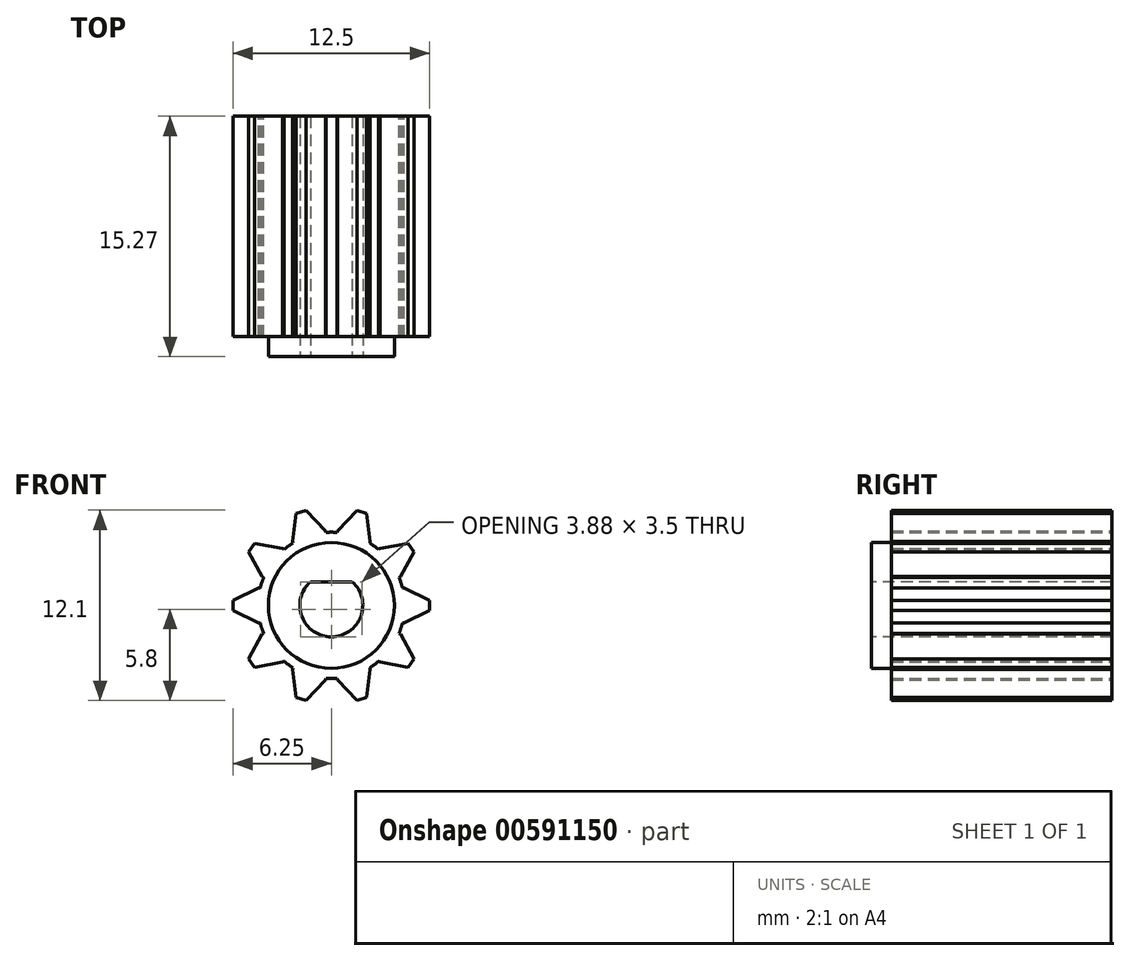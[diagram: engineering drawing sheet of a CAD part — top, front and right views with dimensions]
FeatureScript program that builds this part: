
annotation { "Feature Type Name" : "Feature", "Feature Type Description" : "" }
export const myFeature = defineFeature(function(context is Context, id is Id, definition is map)
    precondition{}
    {
        {
            var Q0;
            Q0=qCreatedBy(makeId("Front.planeOp"),FACE);
            var sketch = newSketch(context, id + "F0", { "sketchPlane" : qUnion([Q0])});
            skCircle(sketch, "E0", {"center": v(0, 0) * mm, "radius": 4.65 * mm});
            skLineSegment(sketch, "E1", {"start": v(0, 0) * mm, "end": v(4.65, 0) * mm, "construction": true});
            skLineSegment(sketch, "E2", {"start": v(4.65, 0) * mm, "end": v(6.25, 0) * mm, "construction": true});
            skLineSegment(sketch, "E3", {"start": v(6.25, 0) * mm, "end": v(6.25, 0.33) * mm});
            skLineSegment(sketch, "E4", {"start": v(4.52, 1.1) * mm, "end": v(4.62, 1.1) * mm});
            skLineSegment(sketch, "E5", {"start": v(4.62, 1.1) * mm, "end": v(6.25, 0.33) * mm});
            skLineSegment(sketch, "E6.MirrorCS", {"start": v(4.62, -1.1) * mm, "end": v(6.25, -0.33) * mm});
            skLineSegment(sketch, "E7.MirrorCS", {"start": v(6.25, 0) * mm, "end": v(6.25, -0.33) * mm});
            skLineSegment(sketch, "E8.MirrorCS", {"start": v(4.52, -1.1) * mm, "end": v(4.62, -1.1) * mm});
            skLineSegment(sketch, "E9.1.0", {"start": v(3, 3.55) * mm, "end": v(3.09, 3.6) * mm});
            skLineSegment(sketch, "E9.1.1", {"start": v(4.3, 1.77) * mm, "end": v(4.38, 1.82) * mm});
            skLineSegment(sketch, "E9.1.2", {"start": v(4.38, 1.82) * mm, "end": v(5.25, 3.4) * mm});
            skLineSegment(sketch, "E9.1.3", {"start": v(3.09, 3.6) * mm, "end": v(4.86, 3.94) * mm});
            skLineSegment(sketch, "E9.1.4", {"start": v(5.06, 3.67) * mm, "end": v(4.86, 3.94) * mm});
            skLineSegment(sketch, "E9.1.5", {"start": v(5.06, 3.67) * mm, "end": v(5.25, 3.4) * mm});
            skLineSegment(sketch, "E9.2.0", {"start": v(0.35, 4.64) * mm, "end": v(0.38, 4.73) * mm});
            skLineSegment(sketch, "E9.2.1", {"start": v(2.44, 3.96) * mm, "end": v(2.47, 4.05) * mm});
            skLineSegment(sketch, "E9.2.2", {"start": v(2.47, 4.05) * mm, "end": v(2.25, 5.84) * mm});
            skLineSegment(sketch, "E9.2.3", {"start": v(0.38, 4.73) * mm, "end": v(1.62, 6.05) * mm});
            skLineSegment(sketch, "E9.2.4", {"start": v(1.93, 5.94) * mm, "end": v(1.62, 6.05) * mm});
            skLineSegment(sketch, "E9.2.5", {"start": v(1.93, 5.94) * mm, "end": v(2.25, 5.84) * mm});
            skLineSegment(sketch, "E9.3.0", {"start": v(-2.44, 3.96) * mm, "end": v(-2.47, 4.05) * mm});
            skLineSegment(sketch, "E9.3.1", {"start": v(-0.35, 4.64) * mm, "end": v(-0.38, 4.73) * mm});
            skLineSegment(sketch, "E9.3.2", {"start": v(-0.38, 4.73) * mm, "end": v(-1.62, 6.05) * mm});
            skLineSegment(sketch, "E9.3.3", {"start": v(-2.47, 4.05) * mm, "end": v(-2.25, 5.84) * mm});
            skLineSegment(sketch, "E9.3.4", {"start": v(-1.93, 5.94) * mm, "end": v(-2.25, 5.84) * mm});
            skLineSegment(sketch, "E9.3.5", {"start": v(-1.93, 5.94) * mm, "end": v(-1.62, 6.05) * mm});
            skLineSegment(sketch, "E9.4.0", {"start": v(-4.3, 1.77) * mm, "end": v(-4.38, 1.82) * mm});
            skLineSegment(sketch, "E9.4.1", {"start": v(-3, 3.55) * mm, "end": v(-3.09, 3.6) * mm});
            skLineSegment(sketch, "E9.4.2", {"start": v(-3.09, 3.6) * mm, "end": v(-4.86, 3.94) * mm});
            skLineSegment(sketch, "E9.4.3", {"start": v(-4.38, 1.82) * mm, "end": v(-5.25, 3.4) * mm});
            skLineSegment(sketch, "E9.4.4", {"start": v(-5.06, 3.67) * mm, "end": v(-5.25, 3.4) * mm});
            skLineSegment(sketch, "E9.4.5", {"start": v(-5.06, 3.67) * mm, "end": v(-4.86, 3.94) * mm});
            skLineSegment(sketch, "E9.5.0", {"start": v(-4.52, -1.1) * mm, "end": v(-4.62, -1.1) * mm});
            skLineSegment(sketch, "E9.5.1", {"start": v(-4.52, 1.1) * mm, "end": v(-4.62, 1.1) * mm});
            skLineSegment(sketch, "E9.5.2", {"start": v(-4.62, 1.1) * mm, "end": v(-6.25, 0.33) * mm});
            skLineSegment(sketch, "E9.5.3", {"start": v(-4.62, -1.1) * mm, "end": v(-6.25, -0.33) * mm});
            skLineSegment(sketch, "E9.5.4", {"start": v(-6.25, 0) * mm, "end": v(-6.25, -0.33) * mm});
            skLineSegment(sketch, "E9.5.5", {"start": v(-6.25, 0) * mm, "end": v(-6.25, 0.33) * mm});
            skLineSegment(sketch, "E9.6.0", {"start": v(-3, -3.55) * mm, "end": v(-3.09, -3.6) * mm});
            skLineSegment(sketch, "E9.6.1", {"start": v(-4.3, -1.77) * mm, "end": v(-4.38, -1.82) * mm});
            skLineSegment(sketch, "E9.6.2", {"start": v(-4.38, -1.82) * mm, "end": v(-5.25, -3.4) * mm});
            skLineSegment(sketch, "E9.6.3", {"start": v(-3.09, -3.6) * mm, "end": v(-4.86, -3.94) * mm});
            skLineSegment(sketch, "E9.6.4", {"start": v(-5.06, -3.67) * mm, "end": v(-4.86, -3.94) * mm});
            skLineSegment(sketch, "E9.6.5", {"start": v(-5.06, -3.67) * mm, "end": v(-5.25, -3.4) * mm});
            skLineSegment(sketch, "E9.7.0", {"start": v(-0.35, -4.64) * mm, "end": v(-0.38, -4.73) * mm});
            skLineSegment(sketch, "E9.7.1", {"start": v(-2.44, -3.96) * mm, "end": v(-2.47, -4.05) * mm});
            skLineSegment(sketch, "E9.7.2", {"start": v(-2.47, -4.05) * mm, "end": v(-2.25, -5.84) * mm});
            skLineSegment(sketch, "E9.7.3", {"start": v(-0.38, -4.73) * mm, "end": v(-1.62, -6.05) * mm});
            skLineSegment(sketch, "E9.7.4", {"start": v(-1.93, -5.94) * mm, "end": v(-1.62, -6.05) * mm});
            skLineSegment(sketch, "E9.7.5", {"start": v(-1.93, -5.94) * mm, "end": v(-2.25, -5.84) * mm});
            skLineSegment(sketch, "E9.8.0", {"start": v(2.44, -3.96) * mm, "end": v(2.47, -4.05) * mm});
            skLineSegment(sketch, "E9.8.1", {"start": v(0.35, -4.64) * mm, "end": v(0.38, -4.73) * mm});
            skLineSegment(sketch, "E9.8.2", {"start": v(0.38, -4.73) * mm, "end": v(1.62, -6.05) * mm});
            skLineSegment(sketch, "E9.8.3", {"start": v(2.47, -4.05) * mm, "end": v(2.25, -5.84) * mm});
            skLineSegment(sketch, "E9.8.4", {"start": v(1.93, -5.94) * mm, "end": v(2.25, -5.84) * mm});
            skLineSegment(sketch, "E9.8.5", {"start": v(1.93, -5.94) * mm, "end": v(1.62, -6.05) * mm});
            skLineSegment(sketch, "E9.9.0", {"start": v(4.3, -1.77) * mm, "end": v(4.38, -1.82) * mm});
            skLineSegment(sketch, "E9.9.1", {"start": v(3, -3.55) * mm, "end": v(3.09, -3.6) * mm});
            skLineSegment(sketch, "E9.9.2", {"start": v(3.09, -3.6) * mm, "end": v(4.86, -3.94) * mm});
            skLineSegment(sketch, "E9.9.3", {"start": v(4.38, -1.82) * mm, "end": v(5.25, -3.4) * mm});
            skLineSegment(sketch, "E9.9.4", {"start": v(5.06, -3.67) * mm, "end": v(5.25, -3.4) * mm});
            skLineSegment(sketch, "E9.9.5", {"start": v(5.06, -3.67) * mm, "end": v(4.86, -3.94) * mm});
            skSolve(sketch);
        }
        {
            var Q0;
            Q0 = qSketchRegion(id + "F0", true);
            extrude(context, id + "F1", {"entities" : qUnion([Q0]), "depth" : 9 * mm, "offsetDistance" : 25.4 * mm, "hasSecondDirection" : true, "secondDirectionOppositeDirection" : true, "secondDirectionDepth" : 5 * mm});
        }
        {
            var Q0;
            Q0=makeQuery(id+"F1.opExtrude","CAP_FACE",FACE,{"disambiguationData":[OSD([sQuery(id+"F0.wireOp",EDGE,"E0"),sQuery(id+"F0.wireOp",EDGE,"E3"),sQuery(id+"F0.wireOp",EDGE,"E4"),sQuery(id+"F0.wireOp",EDGE,"E5"),sQuery(id+"F0.wireOp",EDGE,"E6.MirrorCS"),sQuery(id+"F0.wireOp",EDGE,"E7.MirrorCS"),sQuery(id+"F0.wireOp",EDGE,"E8.MirrorCS"),sQuery(id+"F0.wireOp",EDGE,"9f6130ec-3d1a-4bbb-9d9a-4e7b52390a97.1.0"),sQuery(id+"F0.wireOp",EDGE,"9f6130ec-3d1a-4bbb-9d9a-4e7b52390a97.1.1"),sQuery(id+"F0.wireOp",EDGE,"9f6130ec-3d1a-4bbb-9d9a-4e7b52390a97.1.2"),sQuery(id+"F0.wireOp",EDGE,"9f6130ec-3d1a-4bbb-9d9a-4e7b52390a97.1.3"),sQuery(id+"F0.wireOp",EDGE,"9f6130ec-3d1a-4bbb-9d9a-4e7b52390a97.1.4"),sQuery(id+"F0.wireOp",EDGE,"9f6130ec-3d1a-4bbb-9d9a-4e7b52390a97.1.5"),sQuery(id+"F0.wireOp",EDGE,"9f6130ec-3d1a-4bbb-9d9a-4e7b52390a97.2.0"),sQuery(id+"F0.wireOp",EDGE,"9f6130ec-3d1a-4bbb-9d9a-4e7b52390a97.2.1"),sQuery(id+"F0.wireOp",EDGE,"9f6130ec-3d1a-4bbb-9d9a-4e7b52390a97.2.2"),sQuery(id+"F0.wireOp",EDGE,"9f6130ec-3d1a-4bbb-9d9a-4e7b52390a97.2.3"),sQuery(id+"F0.wireOp",EDGE,"9f6130ec-3d1a-4bbb-9d9a-4e7b52390a97.2.4"),sQuery(id+"F0.wireOp",EDGE,"9f6130ec-3d1a-4bbb-9d9a-4e7b52390a97.2.5"),sQuery(id+"F0.wireOp",EDGE,"9f6130ec-3d1a-4bbb-9d9a-4e7b52390a97.3.0"),sQuery(id+"F0.wireOp",EDGE,"9f6130ec-3d1a-4bbb-9d9a-4e7b52390a97.3.1"),sQuery(id+"F0.wireOp",EDGE,"9f6130ec-3d1a-4bbb-9d9a-4e7b52390a97.3.2"),sQuery(id+"F0.wireOp",EDGE,"9f6130ec-3d1a-4bbb-9d9a-4e7b52390a97.3.3"),sQuery(id+"F0.wireOp",EDGE,"9f6130ec-3d1a-4bbb-9d9a-4e7b52390a97.3.4"),sQuery(id+"F0.wireOp",EDGE,"9f6130ec-3d1a-4bbb-9d9a-4e7b52390a97.3.5"),sQuery(id+"F0.wireOp",EDGE,"9f6130ec-3d1a-4bbb-9d9a-4e7b52390a97.4.0"),sQuery(id+"F0.wireOp",EDGE,"9f6130ec-3d1a-4bbb-9d9a-4e7b52390a97.4.1"),sQuery(id+"F0.wireOp",EDGE,"9f6130ec-3d1a-4bbb-9d9a-4e7b52390a97.4.2"),sQuery(id+"F0.wireOp",EDGE,"9f6130ec-3d1a-4bbb-9d9a-4e7b52390a97.4.3"),sQuery(id+"F0.wireOp",EDGE,"9f6130ec-3d1a-4bbb-9d9a-4e7b52390a97.4.4"),sQuery(id+"F0.wireOp",EDGE,"9f6130ec-3d1a-4bbb-9d9a-4e7b52390a97.4.5"),sQuery(id+"F0.wireOp",EDGE,"9f6130ec-3d1a-4bbb-9d9a-4e7b52390a97.5.0"),sQuery(id+"F0.wireOp",EDGE,"9f6130ec-3d1a-4bbb-9d9a-4e7b52390a97.5.1"),sQuery(id+"F0.wireOp",EDGE,"9f6130ec-3d1a-4bbb-9d9a-4e7b52390a97.5.2"),sQuery(id+"F0.wireOp",EDGE,"9f6130ec-3d1a-4bbb-9d9a-4e7b52390a97.5.3"),sQuery(id+"F0.wireOp",EDGE,"9f6130ec-3d1a-4bbb-9d9a-4e7b52390a97.5.4"),sQuery(id+"F0.wireOp",EDGE,"9f6130ec-3d1a-4bbb-9d9a-4e7b52390a97.5.5"),sQuery(id+"F0.wireOp",EDGE,"9f6130ec-3d1a-4bbb-9d9a-4e7b52390a97.6.0"),sQuery(id+"F0.wireOp",EDGE,"9f6130ec-3d1a-4bbb-9d9a-4e7b52390a97.6.1"),sQuery(id+"F0.wireOp",EDGE,"9f6130ec-3d1a-4bbb-9d9a-4e7b52390a97.6.2"),sQuery(id+"F0.wireOp",EDGE,"9f6130ec-3d1a-4bbb-9d9a-4e7b52390a97.6.3"),sQuery(id+"F0.wireOp",EDGE,"9f6130ec-3d1a-4bbb-9d9a-4e7b52390a97.6.4"),sQuery(id+"F0.wireOp",EDGE,"9f6130ec-3d1a-4bbb-9d9a-4e7b52390a97.6.5"),sQuery(id+"F0.wireOp",EDGE,"9f6130ec-3d1a-4bbb-9d9a-4e7b52390a97.7.0"),sQuery(id+"F0.wireOp",EDGE,"9f6130ec-3d1a-4bbb-9d9a-4e7b52390a97.7.1"),sQuery(id+"F0.wireOp",EDGE,"9f6130ec-3d1a-4bbb-9d9a-4e7b52390a97.7.2"),sQuery(id+"F0.wireOp",EDGE,"9f6130ec-3d1a-4bbb-9d9a-4e7b52390a97.7.3"),sQuery(id+"F0.wireOp",EDGE,"9f6130ec-3d1a-4bbb-9d9a-4e7b52390a97.7.4"),sQuery(id+"F0.wireOp",EDGE,"9f6130ec-3d1a-4bbb-9d9a-4e7b52390a97.7.5"),sQuery(id+"F0.wireOp",EDGE,"9f6130ec-3d1a-4bbb-9d9a-4e7b52390a97.8.0"),sQuery(id+"F0.wireOp",EDGE,"9f6130ec-3d1a-4bbb-9d9a-4e7b52390a97.8.1"),sQuery(id+"F0.wireOp",EDGE,"9f6130ec-3d1a-4bbb-9d9a-4e7b52390a97.8.2"),sQuery(id+"F0.wireOp",EDGE,"9f6130ec-3d1a-4bbb-9d9a-4e7b52390a97.8.3"),sQuery(id+"F0.wireOp",EDGE,"9f6130ec-3d1a-4bbb-9d9a-4e7b52390a97.8.4"),sQuery(id+"F0.wireOp",EDGE,"9f6130ec-3d1a-4bbb-9d9a-4e7b52390a97.8.5"),sQuery(id+"F0.wireOp",EDGE,"9f6130ec-3d1a-4bbb-9d9a-4e7b52390a97.9.0"),sQuery(id+"F0.wireOp",EDGE,"9f6130ec-3d1a-4bbb-9d9a-4e7b52390a97.9.1"),sQuery(id+"F0.wireOp",EDGE,"9f6130ec-3d1a-4bbb-9d9a-4e7b52390a97.9.2"),sQuery(id+"F0.wireOp",EDGE,"9f6130ec-3d1a-4bbb-9d9a-4e7b52390a97.9.3"),sQuery(id+"F0.wireOp",EDGE,"9f6130ec-3d1a-4bbb-9d9a-4e7b52390a97.9.4"),sQuery(id+"F0.wireOp",EDGE,"9f6130ec-3d1a-4bbb-9d9a-4e7b52390a97.9.5"),sQuery(id+"F0.wireOp",EDGE,"9f6130ec-3d1a-4bbb-9d9a-4e7b52390a97.10.0"),sQuery(id+"F0.wireOp",EDGE,"9f6130ec-3d1a-4bbb-9d9a-4e7b52390a97.10.1"),sQuery(id+"F0.wireOp",EDGE,"9f6130ec-3d1a-4bbb-9d9a-4e7b52390a97.10.2"),sQuery(id+"F0.wireOp",EDGE,"9f6130ec-3d1a-4bbb-9d9a-4e7b52390a97.10.3"),sQuery(id+"F0.wireOp",EDGE,"9f6130ec-3d1a-4bbb-9d9a-4e7b52390a97.10.4"),sQuery(id+"F0.wireOp",EDGE,"9f6130ec-3d1a-4bbb-9d9a-4e7b52390a97.10.5"),sQuery(id+"F0.wireOp",EDGE,"9f6130ec-3d1a-4bbb-9d9a-4e7b52390a97.11.0"),sQuery(id+"F0.wireOp",EDGE,"9f6130ec-3d1a-4bbb-9d9a-4e7b52390a97.11.1"),sQuery(id+"F0.wireOp",EDGE,"9f6130ec-3d1a-4bbb-9d9a-4e7b52390a97.11.2"),sQuery(id+"F0.wireOp",EDGE,"9f6130ec-3d1a-4bbb-9d9a-4e7b52390a97.11.3"),sQuery(id+"F0.wireOp",EDGE,"9f6130ec-3d1a-4bbb-9d9a-4e7b52390a97.11.4"),sQuery(id+"F0.wireOp",EDGE,"9f6130ec-3d1a-4bbb-9d9a-4e7b52390a97.11.5"),sQuery(id+"F0.wireOp",EDGE,"9f6130ec-3d1a-4bbb-9d9a-4e7b52390a97.12.0"),sQuery(id+"F0.wireOp",EDGE,"9f6130ec-3d1a-4bbb-9d9a-4e7b52390a97.12.1"),sQuery(id+"F0.wireOp",EDGE,"9f6130ec-3d1a-4bbb-9d9a-4e7b52390a97.12.2"),sQuery(id+"F0.wireOp",EDGE,"9f6130ec-3d1a-4bbb-9d9a-4e7b52390a97.12.3"),sQuery(id+"F0.wireOp",EDGE,"9f6130ec-3d1a-4bbb-9d9a-4e7b52390a97.12.4"),sQuery(id+"F0.wireOp",EDGE,"9f6130ec-3d1a-4bbb-9d9a-4e7b52390a97.12.5"),sQuery(id+"F0.wireOp",EDGE,"9f6130ec-3d1a-4bbb-9d9a-4e7b52390a97.13.0"),sQuery(id+"F0.wireOp",EDGE,"9f6130ec-3d1a-4bbb-9d9a-4e7b52390a97.13.1"),sQuery(id+"F0.wireOp",EDGE,"9f6130ec-3d1a-4bbb-9d9a-4e7b52390a97.13.2"),sQuery(id+"F0.wireOp",EDGE,"9f6130ec-3d1a-4bbb-9d9a-4e7b52390a97.13.3"),sQuery(id+"F0.wireOp",EDGE,"9f6130ec-3d1a-4bbb-9d9a-4e7b52390a97.13.4"),sQuery(id+"F0.wireOp",EDGE,"9f6130ec-3d1a-4bbb-9d9a-4e7b52390a97.13.5"),sQuery(id+"F0.wireOp",EDGE,"9f6130ec-3d1a-4bbb-9d9a-4e7b52390a97.14.0"),sQuery(id+"F0.wireOp",EDGE,"9f6130ec-3d1a-4bbb-9d9a-4e7b52390a97.14.1"),sQuery(id+"F0.wireOp",EDGE,"9f6130ec-3d1a-4bbb-9d9a-4e7b52390a97.14.2"),sQuery(id+"F0.wireOp",EDGE,"9f6130ec-3d1a-4bbb-9d9a-4e7b52390a97.14.3"),sQuery(id+"F0.wireOp",EDGE,"9f6130ec-3d1a-4bbb-9d9a-4e7b52390a97.14.4"),sQuery(id+"F0.wireOp",EDGE,"9f6130ec-3d1a-4bbb-9d9a-4e7b52390a97.14.5"),sQuery(id+"F0.wireOp",EDGE,"9f6130ec-3d1a-4bbb-9d9a-4e7b52390a97.15.0"),sQuery(id+"F0.wireOp",EDGE,"9f6130ec-3d1a-4bbb-9d9a-4e7b52390a97.15.1"),sQuery(id+"F0.wireOp",EDGE,"9f6130ec-3d1a-4bbb-9d9a-4e7b52390a97.15.2"),sQuery(id+"F0.wireOp",EDGE,"9f6130ec-3d1a-4bbb-9d9a-4e7b52390a97.15.3"),sQuery(id+"F0.wireOp",EDGE,"9f6130ec-3d1a-4bbb-9d9a-4e7b52390a97.15.4"),sQuery(id+"F0.wireOp",EDGE,"9f6130ec-3d1a-4bbb-9d9a-4e7b52390a97.15.5"),sQuery(id+"F0.wireOp",EDGE,"9f6130ec-3d1a-4bbb-9d9a-4e7b52390a97.16.0"),sQuery(id+"F0.wireOp",EDGE,"9f6130ec-3d1a-4bbb-9d9a-4e7b52390a97.16.1"),sQuery(id+"F0.wireOp",EDGE,"9f6130ec-3d1a-4bbb-9d9a-4e7b52390a97.16.2"),sQuery(id+"F0.wireOp",EDGE,"9f6130ec-3d1a-4bbb-9d9a-4e7b52390a97.16.3"),sQuery(id+"F0.wireOp",EDGE,"9f6130ec-3d1a-4bbb-9d9a-4e7b52390a97.16.4"),sQuery(id+"F0.wireOp",EDGE,"9f6130ec-3d1a-4bbb-9d9a-4e7b52390a97.16.5"),sQuery(id+"F0.wireOp",EDGE,"9f6130ec-3d1a-4bbb-9d9a-4e7b52390a97.17.0"),sQuery(id+"F0.wireOp",EDGE,"9f6130ec-3d1a-4bbb-9d9a-4e7b52390a97.17.1"),sQuery(id+"F0.wireOp",EDGE,"9f6130ec-3d1a-4bbb-9d9a-4e7b52390a97.17.2"),sQuery(id+"F0.wireOp",EDGE,"9f6130ec-3d1a-4bbb-9d9a-4e7b52390a97.17.3"),sQuery(id+"F0.wireOp",EDGE,"9f6130ec-3d1a-4bbb-9d9a-4e7b52390a97.17.4"),sQuery(id+"F0.wireOp",EDGE,"9f6130ec-3d1a-4bbb-9d9a-4e7b52390a97.17.5"),sQuery(id+"F0.wireOp",EDGE,"9f6130ec-3d1a-4bbb-9d9a-4e7b52390a97.18.0"),sQuery(id+"F0.wireOp",EDGE,"9f6130ec-3d1a-4bbb-9d9a-4e7b52390a97.18.1"),sQuery(id+"F0.wireOp",EDGE,"9f6130ec-3d1a-4bbb-9d9a-4e7b52390a97.18.2"),sQuery(id+"F0.wireOp",EDGE,"9f6130ec-3d1a-4bbb-9d9a-4e7b52390a97.18.3"),sQuery(id+"F0.wireOp",EDGE,"9f6130ec-3d1a-4bbb-9d9a-4e7b52390a97.18.4"),sQuery(id+"F0.wireOp",EDGE,"9f6130ec-3d1a-4bbb-9d9a-4e7b52390a97.18.5"),sQuery(id+"F0.wireOp",EDGE,"9f6130ec-3d1a-4bbb-9d9a-4e7b52390a97.19.0"),sQuery(id+"F0.wireOp",EDGE,"9f6130ec-3d1a-4bbb-9d9a-4e7b52390a97.19.1"),sQuery(id+"F0.wireOp",EDGE,"9f6130ec-3d1a-4bbb-9d9a-4e7b52390a97.19.2"),sQuery(id+"F0.wireOp",EDGE,"9f6130ec-3d1a-4bbb-9d9a-4e7b52390a97.19.3"),sQuery(id+"F0.wireOp",EDGE,"9f6130ec-3d1a-4bbb-9d9a-4e7b52390a97.19.4"),sQuery(id+"F0.wireOp",EDGE,"9f6130ec-3d1a-4bbb-9d9a-4e7b52390a97.19.5"),sQuery(id+"F0.wireOp",EDGE,"9f6130ec-3d1a-4bbb-9d9a-4e7b52390a97.20.0"),sQuery(id+"F0.wireOp",EDGE,"9f6130ec-3d1a-4bbb-9d9a-4e7b52390a97.20.1"),sQuery(id+"F0.wireOp",EDGE,"9f6130ec-3d1a-4bbb-9d9a-4e7b52390a97.20.2"),sQuery(id+"F0.wireOp",EDGE,"9f6130ec-3d1a-4bbb-9d9a-4e7b52390a97.20.3"),sQuery(id+"F0.wireOp",EDGE,"9f6130ec-3d1a-4bbb-9d9a-4e7b52390a97.20.4"),sQuery(id+"F0.wireOp",EDGE,"9f6130ec-3d1a-4bbb-9d9a-4e7b52390a97.20.5")])],"isStart":false});
            var sketch = newSketch(context, id + "F2", { "sketchPlane" : qUnion([Q0])});
            skCircle(sketch, "E10", {"center": v(0, 0) * mm, "radius": 4 * mm});
            skSolve(sketch);
        }
        {
            var Q0;
            Q0 = qSketchRegion(id + "F2", true);
            extrude(context, id + "F3", {"entities" : qUnion([Q0]), "operationType" : NewBodyOperationType.ADD, "depth" : 1.27 * mm, "offsetDistance" : 25.4 * mm});
        }
        {
            var Q0;
            Q0=makeQuery(id+"F3.opExtrude","CAP_FACE",FACE,{"disambiguationData":[OSD([sQuery(id+"F2.wireOp",EDGE,"E10")])],"isStart":false});
            var sketch = newSketch(context, id + "F4", { "sketchPlane" : qUnion([Q0])});
            skArc(sketch, "E11", {"start": v(-1.32, 1.5) * mm, "mid": v(0, -2) * mm, "end": v(1.32, 1.5) * mm});
            skLineSegment(sketch, "E12", {"start": v(-1.32, 1.5) * mm, "end": v(1.32, 1.5) * mm});
            skSolve(sketch);
        }
        {
            var Q0;
            Q0 = qSketchRegion(id + "F4", true);
            extrude(context, id + "F5", {"entities" : qUnion([Q0]), "operationType" : NewBodyOperationType.REMOVE, "oppositeDirection" : true, "depth" : 25.25 * mm, "offsetDistance" : 25.4 * mm});
        }
    });
